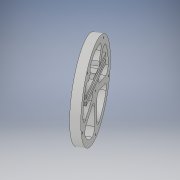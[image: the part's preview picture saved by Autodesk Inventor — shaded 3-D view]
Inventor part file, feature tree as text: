
AUTODESK INVENTOR PART (.ipt)
format: ipt  version: 2017 (Build 210142000, 142)  size: 518,656 bytes
history: native  units: in
note: dims shown in document units (in); Inventor stores cm internally (conversion verified against a paired STEP export)
features: extrude x15, sketch x15, projected_geometry x12, plane x1, imported_body x1
ambient origin geometry x8: Origin, YZ Plane, XZ Plane, XY Plane, X Axis, Y Axis, Z Axis, Center Point
bodies: Solid1 (feature_tree)
feature tree (44):
  extrude  "Extrusion1"  Depth=0.3937in TaperAngle=0.0deg
  extrude  "Extrusion2"  Depth=0.375in
  extrude  "Extrusion3"  Depth=0.125in
  extrude  "Extrusion4"  Depth=0.3937in TaperAngle=0.0deg
  extrude  "Extrusion5"  Depth=0.7087in
  plane  "Work Plane1"
  extrude  "Extrusion6"  Depth=0.9154in
  extrude  "Extrusion7"  Depth=0.1969in
  extrude  "Extrusion8"  Depth=1.3091in
  extrude  "Extrusion9"  Depth=0.0787in TaperAngle=0.0deg
  extrude  "Extrusion10"  Depth=0.125in
  extrude  "Extrusion11"  Depth=0.0787in TaperAngle=0.0deg
  extrude  "Extrusion12"  TaperAngle=90.0deg  [1 undecoded]
  extrude  "Extrusion13"  Depth=0.0787in TaperAngle=0.0deg
  extrude  "Extrusion14"  Depth=0.338in
  extrude  "Extrusion16"  Depth=0.0591in
  sketch  "Sketch1"  dims[d0=1.25in d1=0.0in d2=0.3937in d3=0.0in]
  projected_geometry  "Projected Loop1"
  projected_geometry  "Projected Loop2"
  projected_geometry  "Projected Loop3"
  sketch  "Sketch2"  dims[d4=0.1969in d5=0.0in d6=0.375in]
  sketch  "Sketch3"  dims[d7=0.5in d8=0.125in]
  projected_geometry  "Projected Loop4"
  sketch  "Sketch4"  dims[d9=0.3937in d10=0.0in d11=0.1875in d12=0.0in]
  sketch  "Sketch5"  dims[d13=3.2677in d19=0.7087in]
  projected_geometry  "Projected Loop5"
  sketch  "Sketch8"  dims[d20=0.6102in d21=0.9154in]
  sketch  "Sketch9"  dims[d22=0.6102in d23=0.1969in]
  sketch  "Sketch11"  dims[d24=0.0787in d25=1.3091in]
  sketch  "Sketch13"  dims[d26=0.6693in d27=0.0in d28=0.0787in d29=0.0in]
  projected_geometry  "Projected Loop8"
  sketch  "Sketch14"  dims[d30=0.0787in d31=0.0in d32=0.125in]
  projected_geometry  "Projected Loop9"
  sketch  "Sketch17"  dims[d33=0.0in d34=0.0787in d35=0.0in]
  projected_geometry  "Projected Loop10"
  sketch  "Sketch18"  dims[d36=0.0787in d37=90.0deg]
  sketch  "Sketch19"  dims[d38=0.5118in d39=0.0787in d40=0.0in]
  projected_geometry  "Projected Loop11"
  projected_geometry  "Projected Loop12"
  projected_geometry  "Projected Loop13"
  sketch  "Sketch20"  dims[d41=1.378in d42=0.0in d43=0.338in]
  projected_geometry  "Projected Loop14"
  sketch  "Sketch22"  dims[d44=1.0825in d45=0.0591in d46=1.378in d47=0.0in d48=2.1654in d49=0.75in d50=0.1181in d51=0.1181in d52=0.0in d53=0.1181in d54=0.0in d57=0.3937in d58=0.0in]
  imported_body  "Base1"
note: 1 required parameter value undecoded (feature->parameter linkage not recoverable at this tier; creation-order binding heuristic only, values carry confidence <= 0.55)
